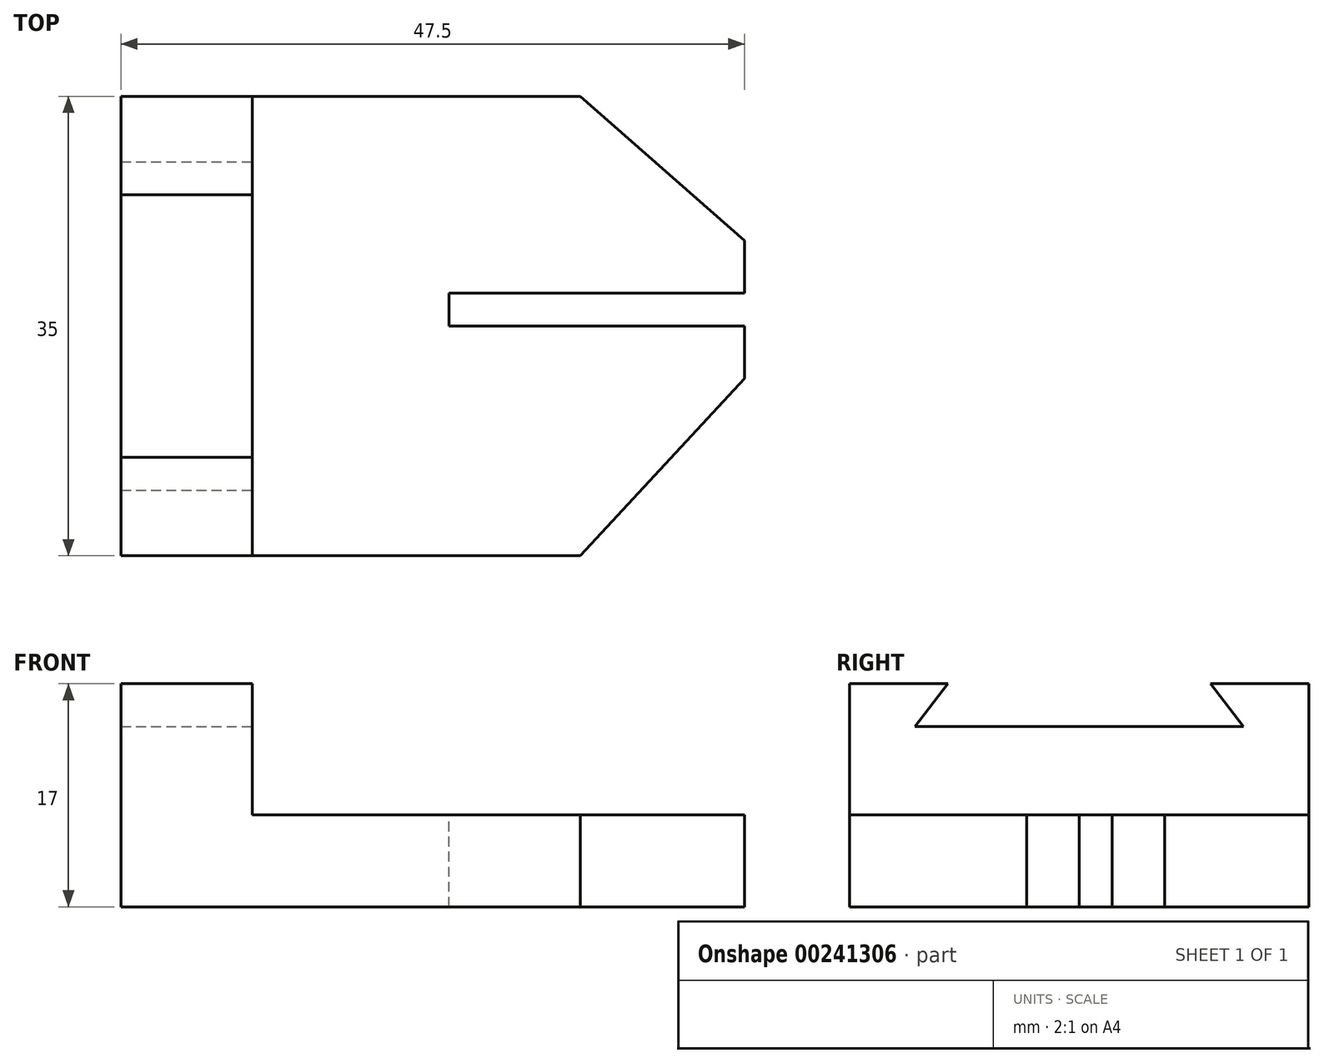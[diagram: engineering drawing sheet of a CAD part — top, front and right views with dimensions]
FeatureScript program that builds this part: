
annotation { "Feature Type Name" : "Feature", "Feature Type Description" : "" }
export const myFeature = defineFeature(function(context is Context, id is Id, definition is map)
    precondition{}
    {
        {
            var Q0;
            Q0=qCreatedBy(makeId("Top.planeOp"),FACE);
            var sketch = newSketch(context, id + "F0", { "sketchPlane" : qUnion([Q0])});
            skLineSegment(sketch, "E0.bottom", {"start": v(-102.85, 8.5) * mm, "end": v(-55.35, 8.5) * mm});
            skLineSegment(sketch, "E0.top", {"start": v(-102.85, -26.5) * mm, "end": v(-55.35, -26.5) * mm});
            skLineSegment(sketch, "E0.left", {"start": v(-102.85, 8.5) * mm, "end": v(-102.85, -26.5) * mm});
            skLineSegment(sketch, "E0.right", {"start": v(-55.35, 8.5) * mm, "end": v(-55.35, -26.5) * mm});
            skSolve(sketch);
        }
        {
            var Q0;
            Q0 = qSketchRegion(id + "F0", true);
            extrude(context, id + "F1", {"entities" : qUnion([Q0]), "depth" : 17 * mm});
        }
        {
            var Q0;
            Q0=makeQuery(id+"F1.opExtrude","CAP_FACE",FACE,{"disambiguationData":[OSD([sQuery(id+"F0.wireOp",EDGE,"E0.bottom"),sQuery(id+"F0.wireOp",EDGE,"E0.top"),sQuery(id+"F0.wireOp",EDGE,"E0.left"),sQuery(id+"F0.wireOp",EDGE,"E0.right")])],"isStart":false});
            var sketch = newSketch(context, id + "F2", { "sketchPlane" : qUnion([Q0])});
            skLineSegment(sketch, "E1.bottom", {"start": v(-102.85, 8.5) * mm, "end": v(-92.85, 8.5) * mm});
            skLineSegment(sketch, "E1.top", {"start": v(-102.85, -26.5) * mm, "end": v(-92.85, -26.5) * mm});
            skLineSegment(sketch, "E1.left", {"start": v(-102.85, 8.5) * mm, "end": v(-102.85, -26.5) * mm});
            skLineSegment(sketch, "E1.right", {"start": v(-92.85, 8.5) * mm, "end": v(-92.85, -26.5) * mm});
            skSolve(sketch);
        }
        {
            var Q0;
            {var subQ0=sQuery(id+"F2.wireOp",EDGE,"E1.right");Q0=makeQuery(id+"F2.imprint","IMPRINT",FACE,{"disambiguationData":[TD([[makeQuery(id+"F2.imprint","IMPRINT",EDGE,{"derivedFrom":subQ0}),1.0]])]});}
            extrude(context, id + "F3", {"entities" : qUnion([Q0]), "operationType" : NewBodyOperationType.REMOVE, "oppositeDirection" : true, "depth" : 10 * mm});
        }
        {
            var Q0;
            Q0=makeQuery(id+"F3.boolean.opBoolean","COPY",FACE,{"derivedFrom":makeQuery(id+"F3.opExtrude","SWEPT_FACE",FACE,{"disambiguationData":[OSD([sQuery(id+"F2.wireOp",EDGE,"E1.right")])]})});
            var sketch = newSketch(context, id + "F4", { "sketchPlane" : qUnion([Q0])});
            skLineSegment(sketch, "E2", {"start": v(-19, 17) * mm, "end": v(-21.5, 13.75) * mm});
            skLineSegment(sketch, "E3", {"start": v(-21.5, 13.75) * mm, "end": v(3.5, 13.75) * mm});
            skLineSegment(sketch, "E4", {"start": v(3.5, 13.75) * mm, "end": v(1, 17) * mm});
            skSolve(sketch);
        }
        {
            var Q0;
            Q0 = qSketchRegion(id + "F4", true);
            var Q1;
            {var subQ0=sQuery(id+"F4.wireOp",EDGE,"E2");Q1=makeQuery(id+"F4.imprint","IMPRINT",FACE,{"disambiguationData":[TD([[makeQuery(id+"F4.imprint","IMPRINT",EDGE,{"derivedFrom":subQ0}),1.0]])]});}
            extrude(context, id + "F5", {"entities" : qUnion([Q0, Q1]), "operationType" : NewBodyOperationType.REMOVE, "endBound" : BoundingType.THROUGH_ALL, "oppositeDirection" : true, "depth" : 25 * mm});
        }
        {
            var Q0;
            Q0=makeQuery(id+"F3.boolean.opBoolean","COPY",FACE,{"derivedFrom":makeQuery(id+"F3.opExtrude","CAP_FACE",FACE,{"disambiguationData":[OSD([sQuery(id+"F0.wireOp",EDGE,"E0.bottom"),sQuery(id+"F0.wireOp",EDGE,"E0.top"),sQuery(id+"F0.wireOp",EDGE,"E0.right"),sQuery(id+"F2.wireOp",EDGE,"E1.right")])],"isStart":false})});
            var sketch = newSketch(context, id + "F6", { "sketchPlane" : qUnion([Q0])});
            skPoint(sketch, "E5.firstSnap0", {"position": v(-92.85, -9) * mm});
            skLineSegment(sketch, "E5.bottom", {"start": v(-77.85, -9) * mm, "end": v(-55.35, -9) * mm});
            skLineSegment(sketch, "E5.top", {"start": v(-77.85, -6.5) * mm, "end": v(-55.35, -6.5) * mm});
            skLineSegment(sketch, "E5.left", {"start": v(-77.85, -9) * mm, "end": v(-77.85, -6.5) * mm});
            skLineSegment(sketch, "E5.right", {"start": v(-55.35, -9) * mm, "end": v(-55.35, -6.5) * mm});
            skSolve(sketch);
        }
        {
            var Q0;
            Q0=makeQuery(id+"F6.imprint","IMPRINT",FACE,{"disambiguationData":[TD([[makeQuery(id+"F6.imprint","IMPRINT",EDGE,{"derivedFrom":sQuery(id+"F6.wireOp",EDGE,"E5.bottom")}),1.0]])]});
            extrude(context, id + "F7", {"entities" : qUnion([Q0]), "operationType" : NewBodyOperationType.REMOVE, "endBound" : BoundingType.THROUGH_ALL, "oppositeDirection" : true, "depth" : 25 * mm});
        }
        {
            var Q0;
            Q0=makeQuery(id+"F3.boolean.opBoolean","COPY",FACE,{"derivedFrom":makeQuery(id+"F3.opExtrude","CAP_FACE",FACE,{"disambiguationData":[OSD([sQuery(id+"F0.wireOp",EDGE,"E0.bottom"),sQuery(id+"F0.wireOp",EDGE,"E0.top"),sQuery(id+"F0.wireOp",EDGE,"E0.right"),sQuery(id+"F2.wireOp",EDGE,"E1.right")])],"isStart":false})});
            var sketch = newSketch(context, id + "F8", { "sketchPlane" : qUnion([Q0])});
            skLineSegment(sketch, "E6", {"start": v(-55.35, -13) * mm, "end": v(-67.85, -26.5) * mm});
            skLineSegment(sketch, "E7", {"start": v(-55.35, -2.5) * mm, "end": v(-67.85, 8.5) * mm});
            skSolve(sketch);
        }
        {
            var Q0;
            Q0 = qSketchRegion(id + "F8", true);
            var Q1;
            {var subQ0=sQuery(id+"F8.wireOp",EDGE,"E7");Q1=makeQuery(id+"F8.imprint","IMPRINT",FACE,{"disambiguationData":[TD([[makeQuery(id+"F8.imprint","IMPRINT",EDGE,{"derivedFrom":subQ0}),-1.0]])]});}
            extrude(context, id + "F9", {"entities" : qUnion([Q0, Q1]), "operationType" : NewBodyOperationType.REMOVE, "endBound" : BoundingType.THROUGH_ALL, "oppositeDirection" : true, "depth" : 25 * mm});
        }
        {
            var Q0;
            Q0=makeQuery(id+"F3.boolean.opBoolean","COPY",FACE,{"derivedFrom":makeQuery(id+"F3.opExtrude","CAP_FACE",FACE,{"disambiguationData":[OSD([sQuery(id+"F0.wireOp",EDGE,"E0.bottom"),sQuery(id+"F0.wireOp",EDGE,"E0.top"),sQuery(id+"F0.wireOp",EDGE,"E0.right"),sQuery(id+"F2.wireOp",EDGE,"E1.right")])],"isStart":false})});
            var sketch = newSketch(context, id + "F10", { "sketchPlane" : qUnion([Q0])});
            skLineSegment(sketch, "E8", {"start": v(-55.35, -13) * mm, "end": v(-67.85, -26.5) * mm});
            skSolve(sketch);
        }
        {
            var Q0;
            Q0 = qSketchRegion(id + "F10", true);
            var Q1;
            {var subQ0=sQuery(id+"F10.wireOp",EDGE,"E8");Q1=makeQuery(id+"F10.imprint","IMPRINT",FACE,{"disambiguationData":[TD([[makeQuery(id+"F10.imprint","IMPRINT",EDGE,{"derivedFrom":subQ0}),1.0]])]});}
            extrude(context, id + "F11", {"entities" : qUnion([Q0, Q1]), "operationType" : NewBodyOperationType.REMOVE, "endBound" : BoundingType.THROUGH_ALL, "oppositeDirection" : true, "depth" : 25 * mm});
        }
    });
